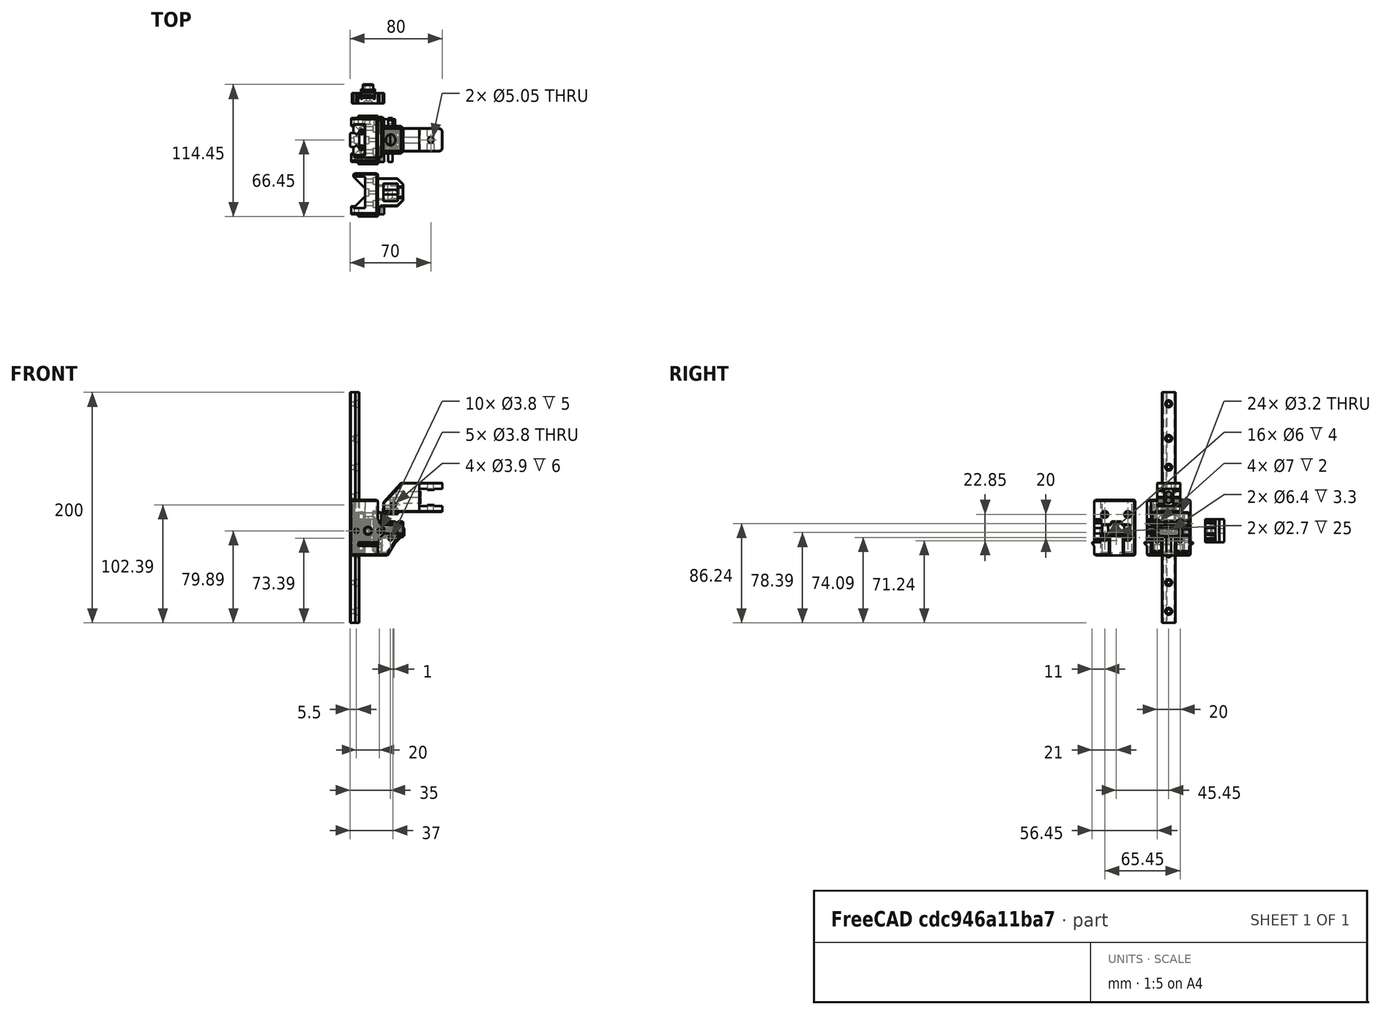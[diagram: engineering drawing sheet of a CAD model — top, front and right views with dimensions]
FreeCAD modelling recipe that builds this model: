
FCSTD DOCUMENT  (FreeCAD 0.19R24291 (Git))
Label: z-arm-12mm-dowel-pin
License: Other
LicenseURL: GPL3
objects: Part::Box×40, Part::MultiFuse×32, Part::Feature×31, Part::Chamfer×30, Part::Cylinder×27, Part::Cut×23, Part::Refine×3, Part::Fillet×2, Part::Mirroring×2
note: 190 computed .brp shape members not serialized (recipe doc carries the construction recipe); baked Part::Feature solids carry a one-line shape summary decoded from their .brp

FEATURE [Part::Feature] Cut028005001  label="x-slider001"
  Placement = pos=(10,0,0) rot=(0,0,1;0rad)
  shape: bbox 34 x 35 x 34.7 mm, 82 faces (baked)
FEATURE [Part::Box] Box  label="Cube"
  AttacherType = Attacher::AttachEngine3D
  Height = 48.4
  Length = 11
  Placement = pos=(0,-16.5,-3) rot=(0,0,1;0rad)
  Width = 33
FEATURE [Part::Feature] Fusion001001  label="_MGN12-pref"
  Placement = pos=(-7.5,4e-15,38.61) rot=(0,0,-1;1.5708rad)
  shape: bbox 13 x 27 x 200 mm, 427 faces (baked)
FEATURE [Part::Cylinder] Cylinder
  Angle = 360
  AttacherType = Attacher::AttachEngine3D
  Height = 11
  Placement = pos=(-3.9e-15,0,17.35) rot=(0,1,0;1.5708rad)
  Radius = 1.6
FEATURE [Part::Cylinder] Cylinder001
  Angle = 360
  AttacherType = Attacher::AttachEngine3D
  Height = 4
  Placement = pos=(7,0,17.35) rot=(0,1,0;1.5708rad)
  Radius = 3
FEATURE [Part::Box] Box001  label="Cube001"
  AttacherType = Attacher::AttachEngine3D
  Height = 48.4
  Length = 11
  Placement = pos=(-10,-16.5,-3) rot=(0,0,1;0rad)
  Width = 2.9
FEATURE [Part::Box] Box002  label="Cube002"
  AttacherType = Attacher::AttachEngine3D
  Height = 48.4
  Length = 23
  Placement = pos=(-12,13.6,-3) rot=(0,0,1;0rad)
  Width = 5.4
FEATURE [Part::MultiFuse] Fusion
  Placement = pos=(0,10,-4.65) rot=(0,0,1;0rad)
  Shapes = -> [Cylinder001,Cylinder]
FEATURE [Part::Feature] Fusion001002  label="Fusion001"
  Placement = pos=(0,-10,-4.65) rot=(0,0,1;0rad)
  shape: bbox 11 x 6 x 6 mm, 6 faces (baked)
FEATURE [Part::Feature] Fusion001003  label="Fusion002"
  Placement = pos=(0,10,15.35) rot=(0,0,1;0rad)
  shape: bbox 11 x 6 x 6 mm, 6 faces (baked)
FEATURE [Part::Feature] Fusion001004  label="Fusion003"
  Placement = pos=(0,-10,15.35) rot=(0,0,1;0rad)
  shape: bbox 11 x 6 x 6 mm, 6 faces (baked)
FEATURE [Part::Box] Box003  label="Cube003"
  AttacherType = Attacher::AttachEngine3D
  Height = 48.4
  Length = 1.8
  Placement = pos=(-12,12,-3) rot=(0,0,1;0rad)
  Width = 2
FEATURE [Part::Box] Box004  label="Cube004"
  AttacherType = Attacher::AttachEngine3D
  Height = 7
  Length = 10
  Placement = pos=(6.5,13.5,15) rot=(0,0,1;0rad)
  Width = 5.5
FEATURE [Part::Feature] Cut028006001  label="y-slider001"
  Placement = pos=(10,0,0) rot=(0,0,1;0rad)
  shape: bbox 36 x 35 x 34.7 mm, 80 faces (baked)
FEATURE [Part::Cylinder] Cylinder002
  Angle = 360
  AttacherType = Attacher::AttachEngine3D
  Height = 5
  Placement = pos=(12,14,17.5) rot=(-1,0,0;1.5708rad)
  Radius = 1.9
FEATURE [Part::Cylinder] Cylinder003
  Angle = 360
  AttacherType = Attacher::AttachEngine3D
  Height = 5
  Placement = pos=(-8,14,17.5) rot=(-1,0,0;1.5708rad)
  Radius = 1.9
FEATURE [Part::Box] Box005  label="Cube005"
  AttacherType = Attacher::AttachEngine3D
  Height = 15
  Length = 5.5
  Placement = pos=(10,13.5,11) rot=(0,0,1;0rad)
  Width = 5.5
FEATURE [Part::Cylinder] Cylinder004
  Angle = 360
  AttacherType = Attacher::AttachEngine3D
  Height = 5
  Placement = pos=(2,22,17.5) rot=(-1,0,0;1.5708rad)
  Radius = 3.5
FEATURE [Part::Chamfer] Chamfer004013007003
  Base = -> Cylinder004
  Edges = 1 edges r=0.5: [Edge3]
  Placement = pos=(0,-3.5,0) rot=(0,0,1;0rad)
FEATURE [Part::MultiFuse] Fusion001006
  Placement = pos=(0.5,0,1) rot=(0,0,1;0rad)
  Shapes = -> [Chamfer004013007003,Cylinder002,Cylinder003]
FEATURE [Part::Box] Box006  label="Cube006"
  AttacherType = Attacher::AttachEngine3D
  Height = 3
  Length = 17
  Placement = pos=(-6,18,4.5) rot=(0,0,1;0rad)
  Width = 3
FEATURE [Part::Chamfer] Chamfer004013007006
  Base = -> Box006
  Edges = 1 edges r=2: [Edge11]
  Placement = pos=(0,0,1) rot=(0,0,1;0rad)
FEATURE [Part::Feature] Fusion003001  label="belt-holder"
  Placement = pos=(2.5,44,18.5) rot=(1,0,0;1.5708rad)
  shape: bbox 12 x 7 x 20 mm, 88 faces (baked)
FEATURE [Part::Feature] Cut002001  label="belt-clamp-nut"
  Placement = pos=(2.5,51.5,18.5) rot=(-1,0,0;1.5708rad)
  shape: bbox 9 x 5 x 20 mm, 11 faces (baked)
FEATURE [Part::Box] Box008  label="Cube008"
  AttacherType = Attacher::AttachEngine3D
  Height = 2.85
  Length = 11
  Placement = pos=(-10,3.5,-3) rot=(0,0,1;0rad)
  Width = 11
FEATURE [Part::Box] Box009  label="Cube009"
  AttacherType = Attacher::AttachEngine3D
  Height = 2.85
  Length = 11
  Placement = pos=(-10,-14.5,-3) rot=(0,0,1;0rad)
  Width = 11
FEATURE [Part::Chamfer] Chamfer
  Base = -> Box009
  Edges = 1 edges r=10: [Edge3]
FEATURE [Part::Chamfer] Chamfer004013007009
  Base = -> Box008
  Edges = 1 edges r=10: [Edge1]
FEATURE [Part::Box] Box010  label="Cube010"
  AttacherType = Attacher::AttachEngine3D
  Height = 2.85
  Length = 4
  Placement = pos=(-12,12,-3) rot=(0,0,1;0rad)
  Width = 2
FEATURE [Part::Box] Box011  label="Cube011"
  AttacherType = Attacher::AttachEngine3D
  Height = 8
  Length = 22
  Placement = pos=(11,-10,13) rot=(0,0,1;0rad)
  Width = 20
FEATURE [Part::Box] Box012  label="Cube012"
  AttacherType = Attacher::AttachEngine3D
  Height = 8
  Length = 20
  Placement = pos=(11,-12,13) rot=(0,0,1;0rad)
  Width = 24
FEATURE [Part::Feature] Fusion001  label="slider-slot"
  Placement = pos=(20,4e-15,19.5) rot=(0,0,-1;1.5708rad)
  shape: bbox 12.3 x 16.2 x 12.1 mm, 8 faces (baked)
FEATURE [Part::Feature] Fusion004005  label="slider-slot001"
  Placement = pos=(22,2,19.5) rot=(0,0,1;3.14159rad)
  shape: bbox 16.2 x 12.3 x 12.1 mm, 8 faces (baked)
FEATURE [Part::Chamfer] Chamfer004013007011012
  Base = -> Box011
  Edges = 2 edges r=3: [Edge5,Edge7]
FEATURE [Part::Box] Box015  label="Cube015"
  AttacherType = Attacher::AttachEngine3D
  Height = 19
  Length = 20
  Placement = pos=(9.5,-6.5,-3) rot=(0,0,1;0rad)
  Width = 13
FEATURE [Part::MultiFuse] Fusion004010
  Shapes = -> [Fusion,Fusion001003,Fusion001002,Fusion001004]
FEATURE [Part::MultiFuse] Fusion004011
  Shapes = -> [Box002,Box,Box001,Box003,Chamfer004013007009,Chamfer,Box010]
FEATURE [Part::Chamfer] Chamfer004013007011015002
  Base = -> Box004
  Edges = 2 edges r=1: [Edge6,Edge8]
FEATURE [Part::Chamfer] Chamfer004013007011015003
  Base = -> Fusion004011
  Edges = 17 edges r=1: [Edge26,Edge27,Edge31,Edge33,Edge50,Edge57,Edge76,Edge77,Edge89,Edge90,Edge97,Edge100,Edge109,Edge115,Edge116,Edge123,Edge125]
FEATURE [Part::Chamfer] Chamfer004013007011015004
  Base = -> Box005
  Edges = 2 edges r=4: [Edge6,Edge8]
FEATURE [Part::Box] Box016  label="Cube016"
  AttacherType = Attacher::AttachEngine3D
  Height = 20
  Length = 2
  Placement = pos=(10.5,13.5,8.5) rot=(0,0,1;0rad)
  Width = 5.5
FEATURE [Part::Feature] Defeatured003
  shape: bbox 28 x 9 x 20 mm, 43 faces (baked)
FEATURE [Part::Chamfer] Chamfer004013007011015006002  label="belt-connector-rf"
  Base = -> Defeatured003
  Edges = 4 edges r=1.5: [Edge18,Edge41,Edge42,Edge56]
FEATURE [Part::Chamfer] Chamfer004013007011015006003
  Base = -> Box016
  Edges = 2 edges r=1.5: [Edge6,Edge8]
FEATURE [Part::MultiFuse] Fusion004015
  Shapes = -> [Chamfer004013007011015002,Chamfer004013007011015004,Chamfer004013007011015006003,Chamfer004013007006,Chamfer004013007011015003]
FEATURE [Part::Cut] Cut
  Base = -> Fusion004015
  Tool = -> Fusion001006
FEATURE [Part::Cut] Cut028006004005  label="block-base"
  Base = -> Cut
  Tool = -> Fusion004010
FEATURE [Part::Feature] Cut028006004005001  label="block-base001"
  shape: bbox 28.5 x 37.5 x 48.4 mm, 58 faces (baked)
FEATURE [Part::Feature] Cut028006004005002  label="block-base002"
  shape: bbox 28.5 x 37.5 x 48.4 mm, 58 faces (baked)
FEATURE [Part::Cylinder] Cylinder005
  Angle = 360
  AttacherType = Attacher::AttachEngine3D
  Height = 5
  Radius = 5.05
FEATURE [Part::Cylinder] Cylinder006
  Angle = 360
  AttacherType = Attacher::AttachEngine3D
  Height = 2
  Placement = pos=(0,0,3) rot=(0,0,1;0rad)
  Radius = 2.9
FEATURE [Part::Box] Box017  label="Cube017"
  AttacherType = Attacher::AttachEngine3D
  Height = 25
  Length = 31
  Placement = pos=(16,-10,35) rot=(0,0,1;0rad)
  Width = 20
FEATURE [Part::Box] Box018  label="Cube018"
  AttacherType = Attacher::AttachEngine3D
  Height = 5
  Length = 20
  Placement = pos=(47,-10,35) rot=(0,0,1;0rad)
  Width = 20
FEATURE [Part::Box] Box019  label="Cube019"
  AttacherType = Attacher::AttachEngine3D
  Height = 5.9
  Length = 2
  Placement = pos=(46,-10,47) rot=(0,0,1;0rad)
  Width = 6
FEATURE [Part::Cylinder] Cylinder007
  Angle = 360
  AttacherType = Attacher::AttachEngine3D
  Height = 37
  Placement = pos=(14,0,50) rot=(0,1,0;1.5708rad)
  Radius = 2.525
FEATURE [Part::Chamfer] Chamfer004013007011015006005
  Base = -> Box017
  Edges = 1 edges: [Edge2 r1=17 r2=15]
FEATURE [Part::Box] Box020  label="Cube020"
  AttacherType = Attacher::AttachEngine3D
  Height = 5.9
  Length = 2
  Placement = pos=(46,4,47) rot=(0,0,1;0rad)
  Width = 6
FEATURE [Part::Cylinder] Cylinder008
  Angle = 360
  AttacherType = Attacher::AttachEngine3D
  Height = 13
  Placement = pos=(14,0,50) rot=(0,1,0;1.5708rad)
  Radius = 4.75
FEATURE [Part::Box] Box021  label="Cube021"
  AttacherType = Attacher::AttachEngine3D
  Height = 1
  Length = 6
  Placement = pos=(54,-10,40) rot=(0,0,1;0rad)
  Width = 7
FEATURE [Part::MultiFuse] Fusion004019
  Shapes = -> [Cylinder008,Cylinder007]
FEATURE [Part::Fillet] Fillet
  Base = -> Box018
  Edges = 2 edges r=3: [Edge5,Edge7]
FEATURE [Part::Cylinder] Cylinder009
  Angle = 360
  AttacherType = Attacher::AttachEngine3D
  Height = 10
  Placement = pos=(57,0,32) rot=(0,0,1;0rad)
  Radius = 2.525
FEATURE [Part::Box] Box022  label="Cube022"
  AttacherType = Attacher::AttachEngine3D
  Height = 1
  Length = 6
  Placement = pos=(54,3,40) rot=(0,0,1;0rad)
  Width = 7
FEATURE [Part::Box] Box023  label="Cube023"
  AttacherType = Attacher::AttachEngine3D
  Height = 10
  Length = 12
  Placement = pos=(7,-4,28) rot=(0,0,1;0rad)
  Width = 8
FEATURE [Part::Cylinder] Cylinder011
  Angle = 360
  AttacherType = Attacher::AttachEngine3D
  Height = 10
  Placement = pos=(24,-4,41) rot=(1,0,0;1.5708rad)
  Radius = 1.95
FEATURE [Part::Cylinder] Cylinder012
  Angle = 360
  AttacherType = Attacher::AttachEngine3D
  Height = 10
  Placement = pos=(24,14,41) rot=(1,0,0;1.5708rad)
  Radius = 1.95
FEATURE [Part::MultiFuse] Fusion004023
  Shapes = -> [Cylinder011,Cylinder012]
FEATURE [Part::Cylinder] Cylinder014
  Angle = 360
  AttacherType = Attacher::AttachEngine3D
  Height = 10
  Placement = pos=(22,-9,25) rot=(1,0,0;1.5708rad)
  Radius = 1.9
FEATURE [Part::Cylinder] Cylinder015
  Angle = 360
  AttacherType = Attacher::AttachEngine3D
  Height = 10
  Placement = pos=(22,19,25) rot=(1,0,0;1.5708rad)
  Radius = 1.9
FEATURE [Part::MultiFuse] Fusion004018
  Shapes = -> [Box020,Box019]
FEATURE [Part::Chamfer] Chamfer004013007011015006006
  Base = -> Fusion004018
  Edges = 2 edges r=1: [Edge8,Edge20]
FEATURE [Part::MultiFuse] Fusion004020
  Shapes = -> [Box022,Fillet,Box021]
FEATURE [Part::Cut] Cut028006004005004
  Base = -> Fusion004020
  Tool = -> Cylinder009
FEATURE [Part::MultiFuse] Fusion004021
  Shapes = -> [Chamfer004013007011015006005,Chamfer004013007011015006006,Cut028006004005004]
FEATURE [Part::Cylinder] Cylinder016
  Angle = 360
  AttacherType = Attacher::AttachEngine3D
  Height = 5
  Radius = 6.55
FEATURE [Part::Cylinder] Cylinder017
  Angle = 360
  AttacherType = Attacher::AttachEngine3D
  Height = 2
  Placement = pos=(0,0,3) rot=(0,0,1;0rad)
  Radius = 2.65
FEATURE [Part::Cut] Cut028006004005015
  Base = -> Cylinder016
  Placement = pos=(22,0,33) rot=(0,0,1;0rad)
  Tool = -> Cylinder017
FEATURE [Part::Box] Box024  label="Cube024"
  AttacherType = Attacher::AttachEngine3D
  Height = 25
  Length = 31
  Placement = pos=(16,-10,35) rot=(0,0,1;0rad)
  Width = 20
FEATURE [Part::Box] Box025  label="Cube025"
  AttacherType = Attacher::AttachEngine3D
  Height = 5
  Length = 20
  Placement = pos=(47,-10,35) rot=(0,0,1;0rad)
  Width = 20
FEATURE [Part::Box] Box026  label="Cube026"
  AttacherType = Attacher::AttachEngine3D
  Height = 5.9
  Length = 2
  Placement = pos=(46,-10,47) rot=(0,0,1;0rad)
  Width = 6
FEATURE [Part::Cylinder] Cylinder018
  Angle = 360
  AttacherType = Attacher::AttachEngine3D
  Height = 37
  Placement = pos=(14,0,45) rot=(0,1,0;1.5708rad)
  Radius = 2.525
FEATURE [Part::Box] Box027  label="Cube027"
  AttacherType = Attacher::AttachEngine3D
  Height = 5.9
  Length = 2
  Placement = pos=(46,4,47) rot=(0,0,1;0rad)
  Width = 6
FEATURE [Part::MultiFuse] Fusion004032
  Placement = pos=(0,0,-5.1) rot=(0,0,1;0rad)
  Shapes = -> [Box027,Box026]
FEATURE [Part::Cylinder] Cylinder019
  Angle = 360
  AttacherType = Attacher::AttachEngine3D
  Height = 8
  Placement = pos=(14,0,45) rot=(0,1,0;1.5708rad)
  Radius = 4.75
FEATURE [Part::Box] Box028  label="Cube028"
  AttacherType = Attacher::AttachEngine3D
  Height = 1
  Length = 6
  Placement = pos=(54,-10,40) rot=(0,0,1;0rad)
  Width = 7
FEATURE [Part::Fillet] Fillet001
  Base = -> Box025
  Edges = 2 edges r=3: [Edge5,Edge7]
FEATURE [Part::Cylinder] Cylinder020
  Angle = 360
  AttacherType = Attacher::AttachEngine3D
  Height = 10
  Placement = pos=(57,0,32) rot=(0,0,1;0rad)
  Radius = 2.525
FEATURE [Part::Box] Box029  label="Cube029"
  AttacherType = Attacher::AttachEngine3D
  Height = 1
  Length = 6
  Placement = pos=(54,3,40) rot=(0,0,1;0rad)
  Width = 7
FEATURE [Part::Box] Box030  label="Cube030"
  AttacherType = Attacher::AttachEngine3D
  Height = 10
  Length = 12
  Placement = pos=(7,-2,28) rot=(0,0,1;0rad)
  Width = 4
FEATURE [Part::Cylinder] Cylinder021
  Angle = 360
  AttacherType = Attacher::AttachEngine3D
  Height = 10
  Placement = pos=(24,-4,41) rot=(1,0,0;1.5708rad)
  Radius = 1.95
FEATURE [Part::Cylinder] Cylinder022
  Angle = 360
  AttacherType = Attacher::AttachEngine3D
  Height = 10
  Placement = pos=(24,14,41) rot=(1,0,0;1.5708rad)
  Radius = 1.95
FEATURE [Part::MultiFuse] Fusion004031
  Placement = pos=(1,0,0) rot=(0,0,1;0rad)
  Shapes = -> [Cylinder021,Cylinder022]
FEATURE [Part::Cut] Cut028006004005016
  Base = -> Fillet001
  Placement = pos=(0,0,6) rot=(0,0,1;0rad)
  Tool = -> Cylinder020
FEATURE [Part::MultiFuse] Fusion004034
  Placement = pos=(0,0,14) rot=(0,0,1;0rad)
  Shapes = -> [Cut028006004005016,Box028,Box029]
FEATURE [Part::Chamfer] Chamfer004013007011015006009004
  Base = -> Fusion004032
  Edges = 2 edges r=1: [Edge6,Edge18]
  Placement = pos=(0,0,0.1) rot=(0,0,1;0rad)
FEATURE [Part::MultiFuse] Fusion004035
  Shapes = -> [Cylinder019,Cylinder018]
FEATURE [Part::MultiFuse] Fusion004025002
  Placement = pos=(0,0,-5) rot=(0,0,1;0rad)
  Shapes = -> [Cylinder015,Cylinder014]
FEATURE [Part::Cylinder] Cylinder013
  Angle = 360
  AttacherType = Attacher::AttachEngine3D
  Height = 10
  Placement = pos=(22,17,25) rot=(1,0,0;1.5708rad)
  Radius = 1.9
FEATURE [Part::Cylinder] Cylinder010
  Angle = 360
  AttacherType = Attacher::AttachEngine3D
  Height = 14
  Placement = pos=(22,7,12) rot=(1,0,0;1.5708rad)
  Radius = 1.9
FEATURE [Part::Chamfer] Chamfer004013007011015006009007001002  label="supporter-base"
  Base = -> Box015
  Edges = 1 edges: [Edge8 r1=17 r2=10]
FEATURE [Part::Chamfer] Chamfer004013007011015006009007001003
  Base = -> Chamfer004013007011015006009007001002
  Edges = 6 edges r=1: [Edge1,Edge3,Edge5,Edge8,Edge9,Edge13]
FEATURE [Part::Cut] Cut028006004005011004  label="supporter-rf"
  Base = -> Chamfer004013007011015006009007001003
  Tool = -> Cylinder010
FEATURE [Part::Feature] Cut028006004005011004001  label="supporter-rf001"
  shape: bbox 20 x 13 x 19 mm, 14 faces (baked)
FEATURE [Part::Feature] Cut028006004005011004002  label="supporter-rf002"
  shape: bbox 20 x 13 x 19 mm, 14 faces (baked)
FEATURE [Part::Box] Box031  label="Cube031"
  AttacherType = Attacher::AttachEngine3D
  Height = 6.4
  Length = 9.5
  Placement = pos=(-2.25,37.7,15.3) rot=(0,0,1;0rad)
  Width = 8
FEATURE [Part::Cut] Cut028006004005011004003  label="belt-mounter-9mm"
  Base = -> Fusion003001
  Tool = -> Box031
FEATURE [Part::Refine] Cut028006004005011004003001  label="belt-mounter-9mm001"
  Source = -> Cut028006004005011004003
FEATURE [Part::Feature] Cut028006004005011004003001001  label="belt-mounter-9mm002"
  shape: bbox 12 x 7 x 20 mm, 80 faces (baked)
FEATURE [Part::Box] Box032  label="Cube032"
  AttacherType = Attacher::AttachEngine3D
  Height = 8
  Length = 22
  Placement = pos=(11,-12,16) rot=(0,0,1;0rad)
  Width = 24
FEATURE [Part::Chamfer] Chamfer004013007011015006009007001004
  Base = -> Box032
  Edges = 2 edges r=5: [Edge5,Edge7]
FEATURE [Part::Chamfer] Chamfer004013007011015006009007001005  label="extend-arm-base"
  Base = -> Chamfer004013007011015006009007001004
  Edges = 5 edges r=0.4: [Edge1,Edge5,Edge7,Edge8,Edge9]
FEATURE [Part::Feature] Fusion004025013  label="slider-slot002"
  Placement = pos=(24,4e-15,19.5) rot=(0,0,-1;1.5708rad)
  shape: bbox 12.3 x 16.2 x 12.1 mm, 8 faces (baked)
FEATURE [Part::Feature] Chamfer004013007011015006009007001005001  label="extend-arm-base001"
  shape: bbox 22 x 24 x 8 mm, 13 faces (baked)
FEATURE [Part::MultiFuse] Fusion004025014
  Shapes = -> [Fusion004025013,Fusion001]
FEATURE [Part::Cut] Cut028006004005011004003001002
  Base = -> Chamfer004013007011015006009007001005001
  Tool = -> Fusion004025014
FEATURE [Part::MultiFuse] Fusion004025015  label="x-slider-16mm"
  Shapes = -> [Cut028006004005011004003001002,Cut028006004005011004002,Cut028006004005002]
FEATURE [Part::Feature] Chamfer004013007011015006009007001005002  label="extend-arm-base002"
  shape: bbox 22 x 24 x 8 mm, 13 faces (baked)
FEATURE [Part::Feature] Fusion004005001  label="slider-slot003"
  Placement = pos=(22,-2,19.5) rot=(0,0,1;3.14159rad)
  shape: bbox 16.2 x 12.3 x 12.1 mm, 8 faces (baked)
FEATURE [Part::MultiFuse] Fusion004025016
  Shapes = -> [Fusion004005,Fusion004005001]
FEATURE [Part::Cut] Cut028006004005011004003001003
  Base = -> Chamfer004013007011015006009007001005002
  Tool = -> Fusion004025016
FEATURE [Part::MultiFuse] Fusion004025017  label="y-slider-16mm"
  Shapes = -> [Cut028006004005011004003001003,Cut028006004005011004001,Cut028006004005001]
FEATURE [Part::Box] Box033  label="Cube033"
  AttacherType = Attacher::AttachEngine3D
  Height = 8
  Length = 5.5
  Placement = pos=(11,10.5,16) rot=(0,0,1;0rad)
  Width = 3
FEATURE [Part::Chamfer] Chamfer004013007011015006009007001005003
  Base = -> Box033
  Edges = 1 edges r=3: [Edge6]
FEATURE [Part::Feature] Chamfer004013007011015006009007001005003001
  shape: bbox 5.5 x 3 x 8 mm, 7 faces (baked)
FEATURE [Part::MultiFuse] Fusion004025018  label="y-slider-16mm-f1"
  Shapes = -> [Fusion004025017,Chamfer004013007011015006009007001005003]
FEATURE [Part::MultiFuse] Fusion004025019  label="x-slider-16mm-f1"
  Shapes = -> [Fusion004025015,Chamfer004013007011015006009007001005003001]
FEATURE [Part::Box] Box034  label="Cube034"
  AttacherType = Attacher::AttachEngine3D
  Height = 3
  Length = 10
  Placement = pos=(17,-12,23.5) rot=(0,0,1;0rad)
  Width = 5.85
FEATURE [Part::Box] Box035  label="Cube035"
  AttacherType = Attacher::AttachEngine3D
  Height = 3
  Length = 10
  Placement = pos=(17,6.15,23.5) rot=(0,0,1;0rad)
  Width = 5.85
FEATURE [Part::Box] Box036  label="Cube036"
  AttacherType = Attacher::AttachEngine3D
  Height = 3
  Length = 10
  Placement = pos=(28.15,5,23.5) rot=(0,0,-1;1.5708rad)
  Width = 4.85
FEATURE [Part::Cylinder] Cylinder023
  Angle = 360
  AttacherType = Attacher::AttachEngine3D
  Height = 28.3
  Placement = pos=(2e-16,0,17) rot=(0,1,0;1.5708rad)
  Radius = 1.35
FEATURE [Part::Cylinder] Cylinder024
  Angle = 360
  AttacherType = Attacher::AttachEngine3D
  Height = 3.3
  Placement = pos=(2e-16,0,17) rot=(0,1,0;1.5708rad)
  Radius = 3.2
FEATURE [Part::MultiFuse] Fusion004025023  label="m3rf"
  Shapes = -> [Cylinder023,Cylinder024]
FEATURE [Part::Feature] Fusion004025023001  label="m3rf001"
  shape: bbox 28.3 x 6.4 x 6.4 mm, 6 faces (baked)
FEATURE [Part::Feature] Fusion004025023004  label="slider-slot004"
  Placement = pos=(24,4e-15,19.5) rot=(0,0,-1;1.5708rad)
  shape: bbox 12.3 x 16.2 x 12.1 mm, 8 faces (baked)
FEATURE [Part::Cylinder] Cylinder025
  Angle = 360
  AttacherType = Attacher::AttachEngine3D
  Height = 3.3
  Placement = pos=(2e-16,0,17) rot=(0,1,0;1.5708rad)
  Radius = 3.2
FEATURE [Part::Box] Box037  label="Cube037"
  AttacherType = Attacher::AttachEngine3D
  Height = 3
  Length = 10
  Placement = pos=(30.15,5,23.5) rot=(0,0,-1;1.5708rad)
  Width = 2.85
FEATURE [Part::Cylinder] Cylinder026
  Angle = 360
  AttacherType = Attacher::AttachEngine3D
  Height = 28.3
  Placement = pos=(2e-16,0,17) rot=(0,1,0;1.5708rad)
  Radius = 1.35
FEATURE [Part::MultiFuse] Fusion004025023003  label="m3rf002"
  Shapes = -> [Cylinder026,Cylinder025]
FEATURE [Part::Feature] Cut028006004005011004003001006  label="supporter-rf003"
  shape: bbox 20 x 13 x 19 mm, 14 faces (baked)
FEATURE [Part::Chamfer] Chamfer004013007011015006009007001005003009
  Base = -> Box037
  Edges = 2 edges r=1: [Edge2,Edge6]
FEATURE [Part::Chamfer] Chamfer004013007011015006009007001005003008
  Base = -> Chamfer004013007011015006009007001005003009
  Edges = 5 edges r=0.4: [Edge3,Edge10,Edge14,Edge15,Edge16]
FEATURE [Part::Feature] Fusion004025023008  label="slider-slot005"
  Placement = pos=(20,4e-15,19.5) rot=(0,0,-1;1.5708rad)
  shape: bbox 12.3 x 16.2 x 12.1 mm, 8 faces (baked)
FEATURE [Part::MultiFuse] Fusion004025023002
  Shapes = -> [Fusion004025023004,Fusion004025023008]
FEATURE [Part::Feature] Chamfer004013007011015006009007001005003011
  shape: bbox 5.5 x 3 x 8 mm, 7 faces (baked)
FEATURE [Part::Feature] Cut028006004005011004003001009  label="block-base003"
  shape: bbox 28.5 x 37.5 x 48.4 mm, 58 faces (baked)
FEATURE [Part::Feature] Chamfer004013007011015006009007001005003012  label="extend-arm-base003"
  shape: bbox 22 x 24 x 8 mm, 13 faces (baked)
FEATURE [Part::Cut] Cut028006004005011004003001008
  Base = -> Chamfer004013007011015006009007001005003012
  Tool = -> Fusion004025023002
FEATURE [Part::MultiFuse] Fusion004025023006  label="x-slider-16mm001"
  Shapes = -> [Cut028006004005011004003001008,Cut028006004005011004003001006,Cut028006004005011004003001009]
FEATURE [Part::MultiFuse] Fusion004025023007  label="x-slider-16mm-f002"
  Shapes = -> [Fusion004025023006,Chamfer004013007011015006009007001005003011]
FEATURE [Part::MultiFuse] Fusion004025023005
  Shapes = -> [Chamfer004013007011015006009007001005003008,Fusion004025023007]
FEATURE [Part::Cut] Cut028006004005011004003001007
  Base = -> Fusion004025023005
  Tool = -> Fusion004025023003
FEATURE [Part::Box] Box038  label="Cube038"
  AttacherType = Attacher::AttachEngine3D
  Height = 54
  Length = 49
  Placement = pos=(-13,-18.5,-6) rot=(0,0,1;0rad)
  Width = 18.5
FEATURE [Part::Cut] Cut028006004005011004003001010
  Base = -> Cut028006004005011004003001007
  Tool = -> Box038
FEATURE [Part::Feature] Cut028006004005011004003001010001
  shape: bbox 45 x 21 x 48.4 mm, 87 faces (baked)
FEATURE [Part::Mirroring] Part__Mirroring  label="Cut028006004005011004003001010001 (Mirror #1)"
  Base = (0,0,0)
  Normal = (0,1,0)
  Source = -> Cut028006004005011004003001010001
FEATURE [Part::MultiFuse] Fusion004025023009  label="x-slider-r1-f2-dual"
  Shapes = -> [Cut028006004005011004003001010,Part__Mirroring]
FEATURE [Part::Feature] Cut028006004005005001
  Placement = pos=(22,0,33) rot=(0,0,1;0rad)
  shape: bbox 13.1 x 13.1 x 5 mm, 5 faces (baked)
FEATURE [Part::Cut] Cut028006004005011004003001010003
  Base = -> Fusion004021
  Tool = -> Fusion004019
FEATURE [Part::Chamfer] Chamfer004013007011015006009007001005003013
  Base = -> Cut028006004005011004003001010003
  Edges = 1 edges r=1: [Edge3]
FEATURE [Part::Cut] Cut028006004005011004003001010004
  Base = -> Chamfer004013007011015006009007001005003013
  Tool = -> Box023
FEATURE [Part::Cut] Cut028006004005011004003001010005
  Base = -> Cut028006004005011004003001010004
  Tool = -> Fusion004023
FEATURE [Part::Chamfer] Chamfer004013007011015006009007001005003014
  Base = -> Cut028006004005011004003001010005
  Edges = 15 edges r=0.4: [Edge1,Edge3,Edge9,Edge10,Edge11,Edge12,Edge20,Edge23,Edge24,Edge25,Edge47,Edge65,Edge73,Edge74,Edge75]
FEATURE [Part::Feature] Cut028006004005011004003001010002001  label="magnet-slot001"
  Placement = pos=(22,0,33) rot=(0,0,1;0rad)
  shape: bbox 10.1 x 10.1 x 5 mm, 5 faces (baked)
FEATURE [Part::Cut] Cut028006004005011004003001010002002  label="bed-mount-bottom"
  Base = -> Chamfer004013007011015006009007001005003014
  Tool = -> Cut028006004005011004003001010002001
FEATURE [Part::Chamfer] Chamfer004013007011015006009007001005003015
  Base = -> Box024
  Edges = 1 edges r=17: [Edge2]
FEATURE [Part::Chamfer] Chamfer004013007011015006009007001005003016
  Base = -> Chamfer004013007011015006009007001005003015
  Edges = 1 edges r=1: [Edge2]
FEATURE [Part::Chamfer] Chamfer004013007011015006009007001005003017
  Base = -> Fusion004034
  Edges = 5 edges r=0.4: [Edge1,Edge5,Edge6,Edge8,Edge9]
FEATURE [Part::Cut] Cut028006004005011004003001010002003
  Base = -> Chamfer004013007011015006009007001005003016
  Tool = -> Fusion004035
FEATURE [Part::Chamfer] Chamfer004013007011015006009007001005003018
  Base = -> Cut028006004005011004003001010002003
  Edges = 10 edges r=0.4: [Edge1,Edge6,Edge8,Edge9,Edge10,Edge11,Edge14,Edge21,Edge22,Edge23]
FEATURE [Part::Cut] Cut028006004005011004003001010002004
  Base = -> Chamfer004013007011015006009007001005003018
  Tool = -> Fusion004031
FEATURE [Part::MultiFuse] Fusion004025023010
  Shapes = -> [Chamfer004013007011015006009004,Chamfer004013007011015006009007001005003017,Cut028006004005011004003001010002004]
FEATURE [Part::Cut] Cut028006004005011004003001010002005
  Base = -> Fusion004025023010
  Tool = -> Box030
FEATURE [Part::Cut] Cut028006004005011004003001010002007  label="magnet-slot"
  Base = -> Cylinder005
  Placement = pos=(22,0,33) rot=(0,0,1;0rad)
  Tool = -> Cylinder006
FEATURE [Part::Cut] Cut028006004005011004003001010002008  label="bed-mount-top-10x6slot"
  Base = -> Cut028006004005011004003001010002005
  Tool = -> Cut028006004005011004003001010002007
FEATURE [Part::Box] Box039  label="Cube039"
  AttacherType = Attacher::AttachEngine3D
  Height = 5
  Length = 17
  Placement = pos=(13.5,-8.15,19) rot=(0,0,1;0rad)
  Width = 2
FEATURE [Part::Box] Box040  label="Cube040"
  AttacherType = Attacher::AttachEngine3D
  Height = 5
  Length = 2
  Placement = pos=(28.15,-8.5,19) rot=(0,0,1;0rad)
  Width = 17
FEATURE [Part::Box] Box041  label="Cube041"
  AttacherType = Attacher::AttachEngine3D
  Height = 5
  Length = 2
  Placement = pos=(13.85,-8.5,19) rot=(0,0,1;0rad)
  Width = 17
FEATURE [Part::Chamfer] Chamfer004013007011015006009007001005003019
  Base = -> Box036
  Edges = 2 edges r=1: [Edge2,Edge6]
FEATURE [Part::Chamfer] Chamfer004013007011015006009007001005003020
  Base = -> Chamfer004013007011015006009007001005003019
  Edges = 5 edges r=0.4: [Edge3,Edge10,Edge14,Edge15,Edge16]
FEATURE [Part::MultiFuse] Fusion004025023011
  Shapes = -> [Fusion004025019,Box041,Box040,Chamfer004013007011015006009007001005003020]
FEATURE [Part::Cut] Cut028006004005011004003001010002009  label="x-slider-r1-f2-base"
  Base = -> Fusion004025023011
  Tool = -> Fusion004025023
FEATURE [Part::Mirroring] Part__Mirroring001  label="x-slider-r1-f2-12mm-dowel"
  Base = (0,0,0)
  Normal = (0,1,0)
  Source = -> Cut028006004005011004003001010002009
FEATURE [Part::MultiFuse] Fusion004025023012
  Shapes = -> [Box034,Box035]
FEATURE [Part::Chamfer] Chamfer004013007011015006009007001005003021
  Base = -> Fusion004025023012
  Edges = 4 edges r=1: [Edge2,Edge6,Edge14,Edge18]
FEATURE [Part::Chamfer] Chamfer004013007011015006009007001005003022
  Base = -> Chamfer004013007011015006009007001005003021
  Edges = 10 edges r=0.4: [Edge1,Edge5,Edge7,Edge8,Edge9,Edge21,Edge28,Edge32,Edge33,Edge34]
FEATURE [Part::Box] Box042  label="Cube042"
  AttacherType = Attacher::AttachEngine3D
  Height = 5
  Length = 17
  Placement = pos=(13.5,6.15,19) rot=(0,0,1;0rad)
  Width = 2
FEATURE [Part::MultiFuse] Fusion004025023013
  Shapes = -> [Box042,Box039,Chamfer004013007011015006009007001005003022,Fusion004025018]
FEATURE [Part::Cut] Cut028006004005011004003001010002010  label="y-slider-r1-f2-12mm-dowel"
  Base = -> Fusion004025023013
  Tool = -> Fusion004025023001
FEATURE [Part::Refine] Cut028006004005011004003001010002010001  label="y-slider-r1-f2-12mm-dowel001"
  Source = -> Cut028006004005011004003001010002010
FEATURE [Part::Refine] Part__Mirroring001001  label="x-slider-r1-f2-12mm-dowel001"
  Placement = pos=(0,-45.45,0) rot=(0,0,1;0rad)
  Source = -> Part__Mirroring001
